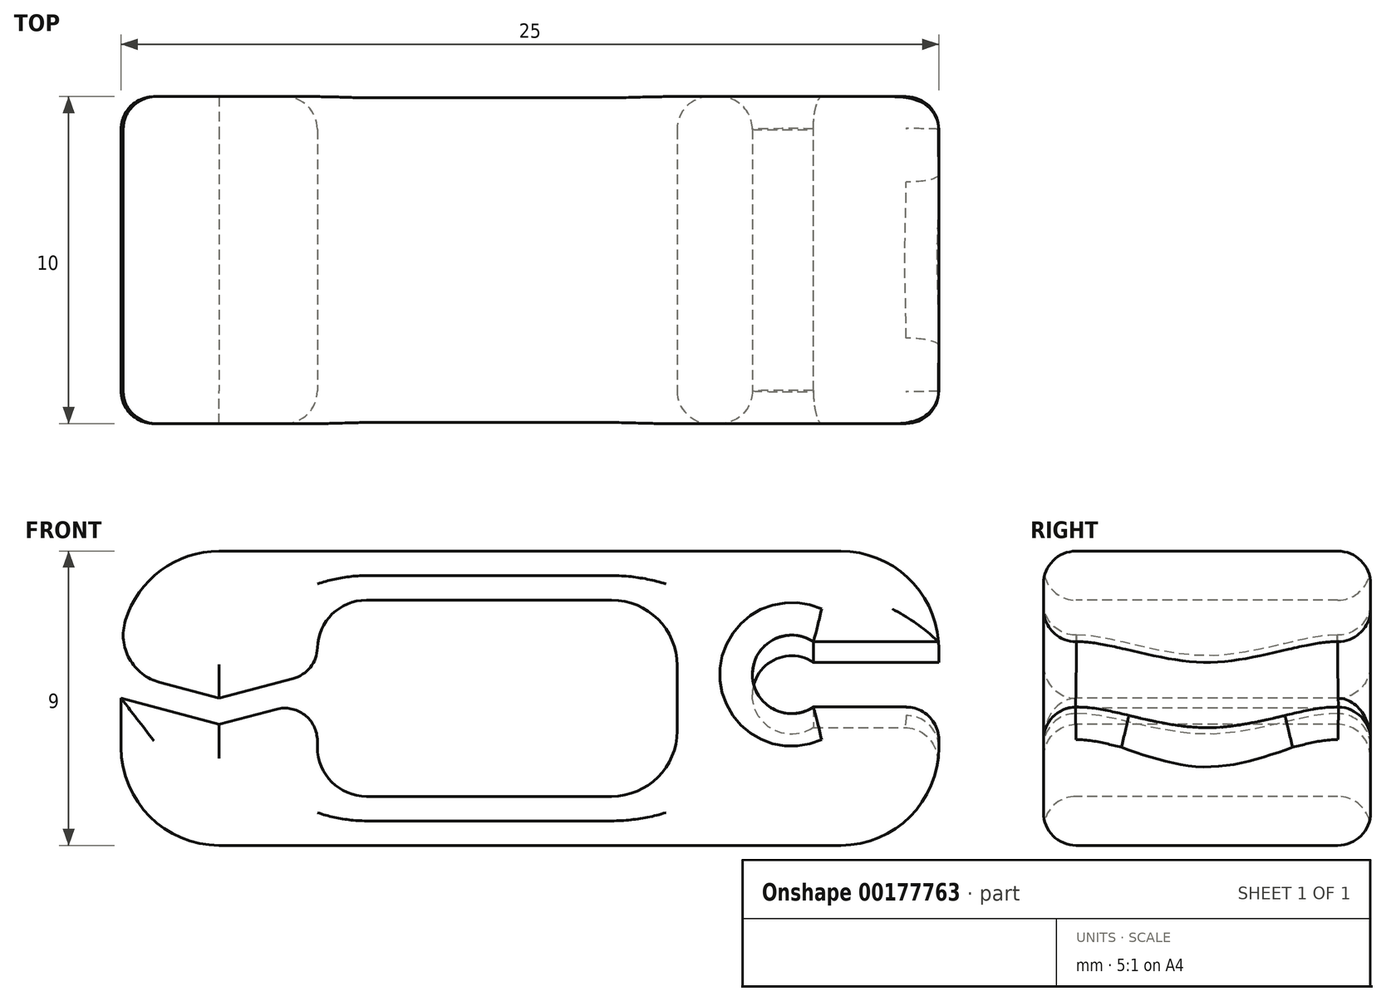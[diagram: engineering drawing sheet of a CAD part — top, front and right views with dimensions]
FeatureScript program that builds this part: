
annotation { "Feature Type Name" : "Feature", "Feature Type Description" : "" }
export const myFeature = defineFeature(function(context is Context, id is Id, definition is map)
    precondition{}
    {
        {
            var Q0;
            Q0=qCreatedBy(makeId("Front.planeOp"),FACE);
            var sketch = newSketch(context, id + "F0", { "sketchPlane" : qUnion([Q0])});
            skLineSegment(sketch, "E0.bottom", {"start": v(0, 0) * mm, "end": v(25, 0) * mm});
            skLineSegment(sketch, "E0.top", {"start": v(0, 9) * mm, "end": v(25, 9) * mm});
            skLineSegment(sketch, "E0.left", {"start": v(0, 0) * mm, "end": v(0, 9) * mm});
            skLineSegment(sketch, "E0.right", {"start": v(25, 0) * mm, "end": v(25, 9) * mm});
            skSolve(sketch);
        }
        {
            var Q0;
            Q0 = qSketchRegion(id + "F0", true);
            extrude(context, id + "F1", {"entities" : qUnion([Q0]), "depth" : 10 * mm});
        }
        {
            var Q0;
            Q0=makeQuery(id+"F1.opExtrude","SWEPT_EDGE",EDGE,{"disambiguationData":[OSD([sQuery(id+"F0.wireOp",EDGE,"E0.bottom"),sQuery(id+"F0.wireOp",EDGE,"E0.left")])]});
            var Q1;
            Q1=makeQuery(id+"F1.opExtrude","SWEPT_EDGE",EDGE,{"disambiguationData":[OSD([sQuery(id+"F0.wireOp",EDGE,"E0.top"),sQuery(id+"F0.wireOp",EDGE,"E0.left")])]});
            var Q2;
            Q2=makeQuery(id+"F1.opExtrude","SWEPT_EDGE",EDGE,{"disambiguationData":[OSD([sQuery(id+"F0.wireOp",EDGE,"E0.bottom"),sQuery(id+"F0.wireOp",EDGE,"E0.right")])]});
            var Q3;
            Q3=makeQuery(id+"F1.opExtrude","SWEPT_EDGE",EDGE,{"disambiguationData":[OSD([sQuery(id+"F0.wireOp",EDGE,"E0.top"),sQuery(id+"F0.wireOp",EDGE,"E0.right")])]});
            fillet(context, id + "F2", {"entities" : qUnion([Q0, Q1, Q2, Q3]), "radius" : 3 * mm, "tangentPropagation" : true, "allowEdgeOverflow" : false});
        }
        {
            var Q0;
            Q0=makeQuery(id+"F1.opExtrude","CAP_FACE",FACE,{"disambiguationData":[OSD([sQuery(id+"F0.wireOp",EDGE,"E0.bottom"),sQuery(id+"F0.wireOp",EDGE,"E0.top"),sQuery(id+"F0.wireOp",EDGE,"E0.left"),sQuery(id+"F0.wireOp",EDGE,"E0.right")])],"isStart":false});
            var sketch = newSketch(context, id + "F3", { "sketchPlane" : qUnion([Q0])});
            skLineSegment(sketch, "E1.bottom", {"start": v(6, 7.5) * mm, "end": v(17, 7.5) * mm});
            skLineSegment(sketch, "E1.top", {"start": v(6, 1.5) * mm, "end": v(17, 1.5) * mm});
            skLineSegment(sketch, "E1.left", {"start": v(6, 7.5) * mm, "end": v(6, 5.3) * mm});
            skLineSegment(sketch, "E1.right", {"start": v(17, 7.5) * mm, "end": v(17, 1.5) * mm});
            skLineSegment(sketch, "E2", {"start": v(0, 4.5) * mm, "end": v(25, 4.5) * mm, "construction": true});
            skLineSegment(sketch, "E3", {"start": v(0, 5.3) * mm, "end": v(3, 4.5) * mm});
            skLineSegment(sketch, "E4", {"start": v(3, 4.5) * mm, "end": v(6, 5.3) * mm});
            skLineSegment(sketch, "E5", {"start": v(0, 4.5) * mm, "end": v(3, 3.7) * mm});
            skLineSegment(sketch, "E6", {"start": v(3, 3.7) * mm, "end": v(6, 4.5) * mm});
            skLineSegment(sketch, "E7.trimOffspring", {"start": v(6, 4.5) * mm, "end": v(6, 1.5) * mm});
            skSolve(sketch);
        }
        {
            var Q0;
            Q0=makeQuery(id+"F3.imprint","IMPRINT",FACE,{"disambiguationData":[TD([[makeQuery(id+"F3.imprint","IMPRINT",EDGE,{"derivedFrom":sQuery(id+"F3.wireOp",EDGE,"E1.bottom")}),-1.0]])]});
            extrude(context, id + "F4", {"entities" : qUnion([Q0]), "operationType" : NewBodyOperationType.REMOVE, "endBound" : BoundingType.THROUGH_ALL, "oppositeDirection" : true, "depth" : 25 * mm});
        }
        {
            var Q0;
            Q0=makeQuery(id+"F4.boolean.opBoolean","COPY",EDGE,{"derivedFrom":makeQuery(id+"F4.opExtrude","SWEPT_EDGE",EDGE,{"disambiguationData":[OSD([sQuery(id+"F3.wireOp",EDGE,"E1.top"),sQuery(id+"F3.wireOp",EDGE,"E1.right")])]})});
            var Q1;
            Q1=makeQuery(id+"F4.boolean.opBoolean","COPY",EDGE,{"derivedFrom":makeQuery(id+"F4.opExtrude","SWEPT_EDGE",EDGE,{"disambiguationData":[OSD([sQuery(id+"F3.wireOp",EDGE,"E1.bottom"),sQuery(id+"F3.wireOp",EDGE,"E1.right")])]})});
            fillet(context, id + "F5", {"entities" : qUnion([Q0, Q1]), "radius" : 2 * mm, "tangentPropagation" : true, "allowEdgeOverflow" : false});
        }
        {
            var Q0;
            Q0=makeQuery(id+"F4.boolean.opBoolean","COPY",EDGE,{"derivedFrom":makeQuery(id+"F4.opExtrude","SWEPT_EDGE",EDGE,{"disambiguationData":[OSD([sQuery(id+"F3.wireOp",EDGE,"E1.bottom"),sQuery(id+"F3.wireOp",EDGE,"E1.left")])]})});
            var Q1;
            Q1=makeQuery(id+"F4.boolean.opBoolean","COPY",EDGE,{"derivedFrom":makeQuery(id+"F4.opExtrude","SWEPT_EDGE",EDGE,{"disambiguationData":[OSD([sQuery(id+"F3.wireOp",EDGE,"E1.top"),sQuery(id+"F3.wireOp",EDGE,"E7.trimOffspring")])]})});
            fillet(context, id + "F6", {"entities" : qUnion([Q0, Q1]), "radius" : 1.5 * mm, "tangentPropagation" : true, "allowEdgeOverflow" : false});
        }
        {
            var Q0;
            Q0=makeQuery(id+"F4.boolean.opBoolean","COPY",EDGE,{"derivedFrom":makeQuery(id+"F4.opExtrude","SWEPT_EDGE",EDGE,{"disambiguationData":[OSD([sQuery(id+"F3.wireOp",EDGE,"E1.left"),sQuery(id+"F3.wireOp",EDGE,"E4")])]})});
            var Q1;
            Q1=makeQuery(id+"F4.boolean.opBoolean","COPY",EDGE,{"derivedFrom":makeQuery(id+"F4.opExtrude","SWEPT_EDGE",EDGE,{"disambiguationData":[OSD([sQuery(id+"F3.wireOp",EDGE,"E6"),sQuery(id+"F3.wireOp",EDGE,"E7.trimOffspring")])]})});
            fillet(context, id + "F7", {"entities" : qUnion([Q0, Q1]), "radius" : 1 * mm, "tangentPropagation" : true, "allowEdgeOverflow" : false});
        }
        {
            var Q0;
            Q0=makeQuery(id+"F4.boolean.opBoolean","COPY",EDGE,{"derivedFrom":makeQuery(id+"F4.opExtrude","SWEPT_EDGE",EDGE,{"disambiguationData":[OSD([sQuery(id+"F0.wireOp",EDGE,"E0.left"),sQuery(id+"F3.wireOp",EDGE,"E3")])]})});
            var Q1;
            Q1=makeQuery(id+"F4.boolean.opBoolean","COPY",EDGE,{"derivedFrom":makeQuery(id+"F4.opExtrude","SWEPT_EDGE",EDGE,{"disambiguationData":[OSD([sQuery(id+"F0.wireOp",EDGE,"E0.left"),sQuery(id+"F3.wireOp",EDGE,"E5")])]})});
            fillet(context, id + "F8", {"entities" : qUnion([Q0, Q1]), "radius" : 1.5 * mm, "tangentPropagation" : true, "allowEdgeOverflow" : false});
        }
        {
            var Q0;
            Q0=makeQuery(id+"F1.opExtrude","CAP_FACE",FACE,{"disambiguationData":[OSD([sQuery(id+"F0.wireOp",EDGE,"E0.bottom"),sQuery(id+"F0.wireOp",EDGE,"E0.top"),sQuery(id+"F0.wireOp",EDGE,"E0.left"),sQuery(id+"F0.wireOp",EDGE,"E0.right")])],"isStart":false});
            var sketch = newSketch(context, id + "F9", { "sketchPlane" : qUnion([Q0])});
            skLineSegment(sketch, "E8.bottom", {"start": v(25, 6) * mm, "end": v(21.16, 6) * mm});
            skLineSegment(sketch, "E8.top", {"start": v(25, 4) * mm, "end": v(21.16, 4) * mm});
            skLineSegment(sketch, "E8.left", {"start": v(25, 6) * mm, "end": v(25, 4) * mm});
            skArc(sketch, "E9", {"start": v(21.16, 6) * mm, "mid": v(19.3, 5) * mm, "end": v(21.16, 4) * mm});
            skPoint(sketch, "E10.orphan", {"position": v(20.5, 6) * mm});
            skPoint(sketch, "E11.orphan", {"position": v(20.5, 4) * mm});
            skSolve(sketch);
        }
        {
            var Q0;
            Q0=makeQuery(id+"F1.opExtrude","SWEPT_FACE",FACE,{"disambiguationData":[OSD([sQuery(id+"F0.wireOp",EDGE,"E0.right")])]});
            var sketch = newSketch(context, id + "F10", { "sketchPlane" : qUnion([Q0])});
            skPoint(sketch, "E12.0", {"position": v(-10, 4) * mm});
            skLineSegment(sketch, "E13", {"start": v(-5, 3) * mm, "end": v(-5, 11.12) * mm, "construction": true});
            skPoint(sketch, "E14", {"position": v(0, 4) * mm});
            skLineSegment(sketch, "E15", {"start": v(-7.5, 3) * mm, "end": v(-7.5, 10.66) * mm, "construction": true});
            skLineSegment(sketch, "E16", {"start": v(-2.5, 3) * mm, "end": v(-2.5, 10.66) * mm, "construction": true});
            skFitSpline(sketch, "E17", {"points": [v(-10, 4) * mm, v(-7.5, 4) * mm, v(-5, 3.6) * mm, v(-2.5, 4) * mm, v(0, 4) * mm], "startDerivative": vector(9.78, 4.82) * mm, "endDerivative": vector(9.78, -4.82) * mm});
            skLineSegment(sketch, "E18", {"start": v(-9.19, 4.4) * mm, "end": v(-0.81, 4.4) * mm, "construction": true});
            skLineSegment(sketch, "E19", {"start": v(-10, 4) * mm, "end": v(0, 4) * mm, "construction": true});
            skSolve(sketch);
        }
        {
            var Q0;
            Q0=makeQuery(id+"F9.imprint","IMPRINT",FACE,{"disambiguationData":[TD([[makeQuery(id+"F9.imprint","IMPRINT",EDGE,{"derivedFrom":sQuery(id+"F9.wireOp",EDGE,"E8.bottom")}),1.0]])]});
            var Q1;
            Q1 = qConstructionFilter(qBodyType(qCreatedBy(id + "F10" ,EDGE), BodyType.WIRE), ConstructionObject.NO);
            sweep(context, id + "F11", {"operationType" : NewBodyOperationType.REMOVE, "profiles" : qUnion([Q0]), "path" : qUnion([Q1]), "keepProfileOrientation" : true});
        }
        {
            var Q0;
            Q0=makeQuery(id+"F1.opExtrude","CAP_FACE",FACE,{"disambiguationData":[OSD([sQuery(id+"F0.wireOp",EDGE,"E0.bottom"),sQuery(id+"F0.wireOp",EDGE,"E0.top"),sQuery(id+"F0.wireOp",EDGE,"E0.left"),sQuery(id+"F0.wireOp",EDGE,"E0.right")])],"isStart":true});
            var Q1;
            Q1=makeQuery(id+"F1.opExtrude","CAP_FACE",FACE,{"disambiguationData":[OSD([sQuery(id+"F0.wireOp",EDGE,"E0.bottom"),sQuery(id+"F0.wireOp",EDGE,"E0.top"),sQuery(id+"F0.wireOp",EDGE,"E0.left"),sQuery(id+"F0.wireOp",EDGE,"E0.right")])],"isStart":false});
            fillet(context, id + "F12", {"entities" : qUnion([Q0, Q1]), "radius" : 1 * mm, "tangentPropagation" : true, "allowEdgeOverflow" : false});
        }
        {
            var Q0;
            {var subQ0=sQuery(id+"F0.wireOp",EDGE,"E0.right");var subQ1=sQuery(id+"F0.wireOp",EDGE,"E0.left");var subQ2=sQuery(id+"F0.wireOp",EDGE,"E0.top");var subQ3=sQuery(id+"F0.wireOp",EDGE,"E0.bottom");var subQ4=sQuery(id+"F10.wireOp",EDGE,"E17");var subQ5=sQuery(id+"F9.wireOp",EDGE,"E8.bottom");Q0=makeQuery(id+"F11.boolean.opBoolean","COPY",EDGE,{"disambiguationData":[TD([makeQuery(id+"F1.opExtrude","CAP_FACE",FACE,{"disambiguationData":[OSD([subQ3,subQ2,subQ1,subQ0])],"isStart":false}),makeQuery(id+"F1.opExtrude","SWEPT_FACE",FACE,{"disambiguationData":[OSD([subQ0])]}),makeQuery(id+"F2.opFillet","BLEND_FACE",FACE,{"disambiguationData":[OSD([subQ2,subQ0])]}),makeQuery(id+"F11.opSweep","SWEPT_FACE",FACE,{"disambiguationData":[OSD([subQ5,subQ4])]})])],"derivedFrom":makeQuery(id+"F11.opSweep","SWEPT_EDGE",EDGE,{"disambiguationData":[OSD([subQ3,subQ2,subQ1,subQ0,subQ5,sQuery(id+"F9.wireOp",EDGE,"E8.left"),subQ4])]})});}
            var Q1;
            {var subQ0=sQuery(id+"F0.wireOp",EDGE,"E0.right");var subQ1=sQuery(id+"F0.wireOp",EDGE,"E0.top");var subQ2=sQuery(id+"F10.wireOp",EDGE,"E17");var subQ3=sQuery(id+"F9.wireOp",EDGE,"E8.bottom");Q1=makeQuery(id+"F11.boolean.opBoolean","COPY",EDGE,{"disambiguationData":[TD([makeQuery(id+"F1.opExtrude","SWEPT_FACE",FACE,{"disambiguationData":[OSD([subQ0])]}),makeQuery(id+"F2.opFillet","BLEND_FACE",FACE,{"disambiguationData":[OSD([subQ1,subQ0])]}),makeQuery(id+"F11.opSweep","SWEPT_FACE",FACE,{"disambiguationData":[OSD([subQ3,subQ2])]})])],"derivedFrom":makeQuery(id+"F11.opSweep","SWEPT_EDGE",EDGE,{"disambiguationData":[OSD([sQuery(id+"F0.wireOp",EDGE,"E0.bottom"),subQ1,sQuery(id+"F0.wireOp",EDGE,"E0.left"),subQ0,subQ3,sQuery(id+"F9.wireOp",EDGE,"E8.left"),subQ2])]})});}
            var Q2;
            {var subQ0=sQuery(id+"F0.wireOp",EDGE,"E0.right");var subQ1=sQuery(id+"F0.wireOp",EDGE,"E0.left");var subQ2=sQuery(id+"F0.wireOp",EDGE,"E0.top");var subQ3=sQuery(id+"F0.wireOp",EDGE,"E0.bottom");var subQ4=sQuery(id+"F10.wireOp",EDGE,"E17");var subQ5=sQuery(id+"F9.wireOp",EDGE,"E8.bottom");Q2=makeQuery(id+"F11.boolean.opBoolean","COPY",EDGE,{"disambiguationData":[TD([makeQuery(id+"F1.opExtrude","CAP_FACE",FACE,{"disambiguationData":[OSD([subQ3,subQ2,subQ1,subQ0])],"isStart":true}),makeQuery(id+"F1.opExtrude","SWEPT_FACE",FACE,{"disambiguationData":[OSD([subQ0])]}),makeQuery(id+"F2.opFillet","BLEND_FACE",FACE,{"disambiguationData":[OSD([subQ2,subQ0])]}),makeQuery(id+"F11.opSweep","SWEPT_FACE",FACE,{"disambiguationData":[OSD([subQ5,subQ4])]})])],"derivedFrom":makeQuery(id+"F11.opSweep","SWEPT_EDGE",EDGE,{"disambiguationData":[OSD([subQ3,subQ2,subQ1,subQ0,subQ5,sQuery(id+"F9.wireOp",EDGE,"E8.left"),subQ4])]})});}
            var Q3;
            {var subQ0=sQuery(id+"F0.wireOp",EDGE,"E0.right");var subQ1=sQuery(id+"F0.wireOp",EDGE,"E0.top");Q3=makeQuery(id+"F12.opFillet","BLEND_EDGE",EDGE,{"blendedFrom":[makeQuery(id+"F2.opFillet","BLEND_EDGE",EDGE,{"blendedFrom":[makeQuery(id+"F1.opExtrude","SWEPT_EDGE",EDGE,{"disambiguationData":[OSD([subQ1,subQ0])]}),makeQuery(id+"F1.opExtrude","CAP_FACE",FACE,{"disambiguationData":[OSD([sQuery(id+"F0.wireOp",EDGE,"E0.bottom"),subQ1,sQuery(id+"F0.wireOp",EDGE,"E0.left"),subQ0])],"isStart":true})],"blendedInto":[makeQuery(id+"F1.opExtrude","CAP_FACE",FACE,{"disambiguationData":[OSD([sQuery(id+"F0.wireOp",EDGE,"E0.bottom"),subQ1,sQuery(id+"F0.wireOp",EDGE,"E0.left"),subQ0])],"isStart":true})]}),makeQuery(id+"F11.boolean.opBoolean","COPY",EDGE,{"derivedFrom":makeQuery(id+"F11.opSweep","CAP_EDGE",EDGE,{"disambiguationData":[OSD([sQuery(id+"F9.wireOp",EDGE,"E8.bottom"),sQuery(id+"F10.wireOp",VERTEX,"E17.end")])],"isStart":false})})],"blendedInto":[]});}
            var Q4;
            {var subQ0=sQuery(id+"F0.wireOp",EDGE,"E0.right");var subQ1=sQuery(id+"F0.wireOp",EDGE,"E0.top");Q4=makeQuery(id+"F12.opFillet","BLEND_EDGE",EDGE,{"blendedFrom":[makeQuery(id+"F2.opFillet","BLEND_EDGE",EDGE,{"blendedFrom":[makeQuery(id+"F1.opExtrude","SWEPT_EDGE",EDGE,{"disambiguationData":[OSD([subQ1,subQ0])]}),makeQuery(id+"F1.opExtrude","CAP_FACE",FACE,{"disambiguationData":[OSD([sQuery(id+"F0.wireOp",EDGE,"E0.bottom"),subQ1,sQuery(id+"F0.wireOp",EDGE,"E0.left"),subQ0])],"isStart":false})],"blendedInto":[makeQuery(id+"F1.opExtrude","CAP_FACE",FACE,{"disambiguationData":[OSD([sQuery(id+"F0.wireOp",EDGE,"E0.bottom"),subQ1,sQuery(id+"F0.wireOp",EDGE,"E0.left"),subQ0])],"isStart":false})]}),makeQuery(id+"F11.boolean.opBoolean","COPY",EDGE,{"derivedFrom":makeQuery(id+"F11.opSweep","CAP_EDGE",EDGE,{"disambiguationData":[OSD([sQuery(id+"F9.wireOp",EDGE,"E8.bottom"),sQuery(id+"F10.wireOp",VERTEX,"E17.start")])],"isStart":true})})],"blendedInto":[]});}
            var Q5;
            Q5=makeQuery(id+"F12.opFillet","BLEND_EDGE",EDGE,{"blendedFrom":[makeQuery(id+"F11.boolean.opBoolean","COPY",EDGE,{"derivedFrom":makeQuery(id+"F11.opSweep","CAP_EDGE",EDGE,{"disambiguationData":[OSD([sQuery(id+"F9.wireOp",EDGE,"E8.top"),sQuery(id+"F10.wireOp",VERTEX,"E17.start")])],"isStart":true})}),makeQuery(id+"F1.opExtrude","CAP_EDGE",EDGE,{"disambiguationData":[OSD([sQuery(id+"F0.wireOp",EDGE,"E0.right")])],"isStart":false})],"blendedInto":[]});
            var Q6;
            {var subQ0=sQuery(id+"F0.wireOp",EDGE,"E0.right");var subQ1=sQuery(id+"F0.wireOp",EDGE,"E0.bottom");var subQ2=sQuery(id+"F10.wireOp",EDGE,"E17");var subQ3=sQuery(id+"F9.wireOp",EDGE,"E8.top");Q6=makeQuery(id+"F11.boolean.opBoolean","COPY",EDGE,{"disambiguationData":[TD([makeQuery(id+"F1.opExtrude","CAP_FACE",FACE,{"disambiguationData":[OSD([subQ1,sQuery(id+"F0.wireOp",EDGE,"E0.top"),sQuery(id+"F0.wireOp",EDGE,"E0.left"),subQ0])],"isStart":false})])],"derivedFrom":makeQuery(id+"F11.opSweep","SWEPT_EDGE",EDGE,{"disambiguationData":[OSD([subQ0,subQ3,sQuery(id+"F9.wireOp",EDGE,"E8.left"),subQ2])]})});}
            var Q7;
            {var subQ0=sQuery(id+"F0.wireOp",EDGE,"E0.right");var subQ1=sQuery(id+"F0.wireOp",EDGE,"E0.bottom");var subQ2=sQuery(id+"F10.wireOp",EDGE,"E17");var subQ3=sQuery(id+"F9.wireOp",EDGE,"E8.top");Q7=makeQuery(id+"F11.boolean.opBoolean","COPY",EDGE,{"disambiguationData":[TD([makeQuery(id+"F1.opExtrude","CAP_FACE",FACE,{"disambiguationData":[OSD([subQ1,sQuery(id+"F0.wireOp",EDGE,"E0.top"),sQuery(id+"F0.wireOp",EDGE,"E0.left"),subQ0])],"isStart":true})])],"derivedFrom":makeQuery(id+"F11.opSweep","SWEPT_EDGE",EDGE,{"disambiguationData":[OSD([subQ0,subQ3,sQuery(id+"F9.wireOp",EDGE,"E8.left"),subQ2])]})});}
            var Q8;
            Q8=makeQuery(id+"F12.opFillet","BLEND_EDGE",EDGE,{"blendedFrom":[makeQuery(id+"F11.boolean.opBoolean","COPY",EDGE,{"derivedFrom":makeQuery(id+"F11.opSweep","CAP_EDGE",EDGE,{"disambiguationData":[OSD([sQuery(id+"F9.wireOp",EDGE,"E8.top"),sQuery(id+"F10.wireOp",VERTEX,"E17.end")])],"isStart":false})}),makeQuery(id+"F1.opExtrude","CAP_EDGE",EDGE,{"disambiguationData":[OSD([sQuery(id+"F0.wireOp",EDGE,"E0.right")])],"isStart":true})],"blendedInto":[]});
            fillet(context, id + "F13", {"entities" : qUnion([Q0, Q1, Q2, Q3, Q4, Q5, Q6, Q7, Q8]), "radius" : 1 * mm, "tangentPropagation" : true, "allowEdgeOverflow" : false});
        }
    });
